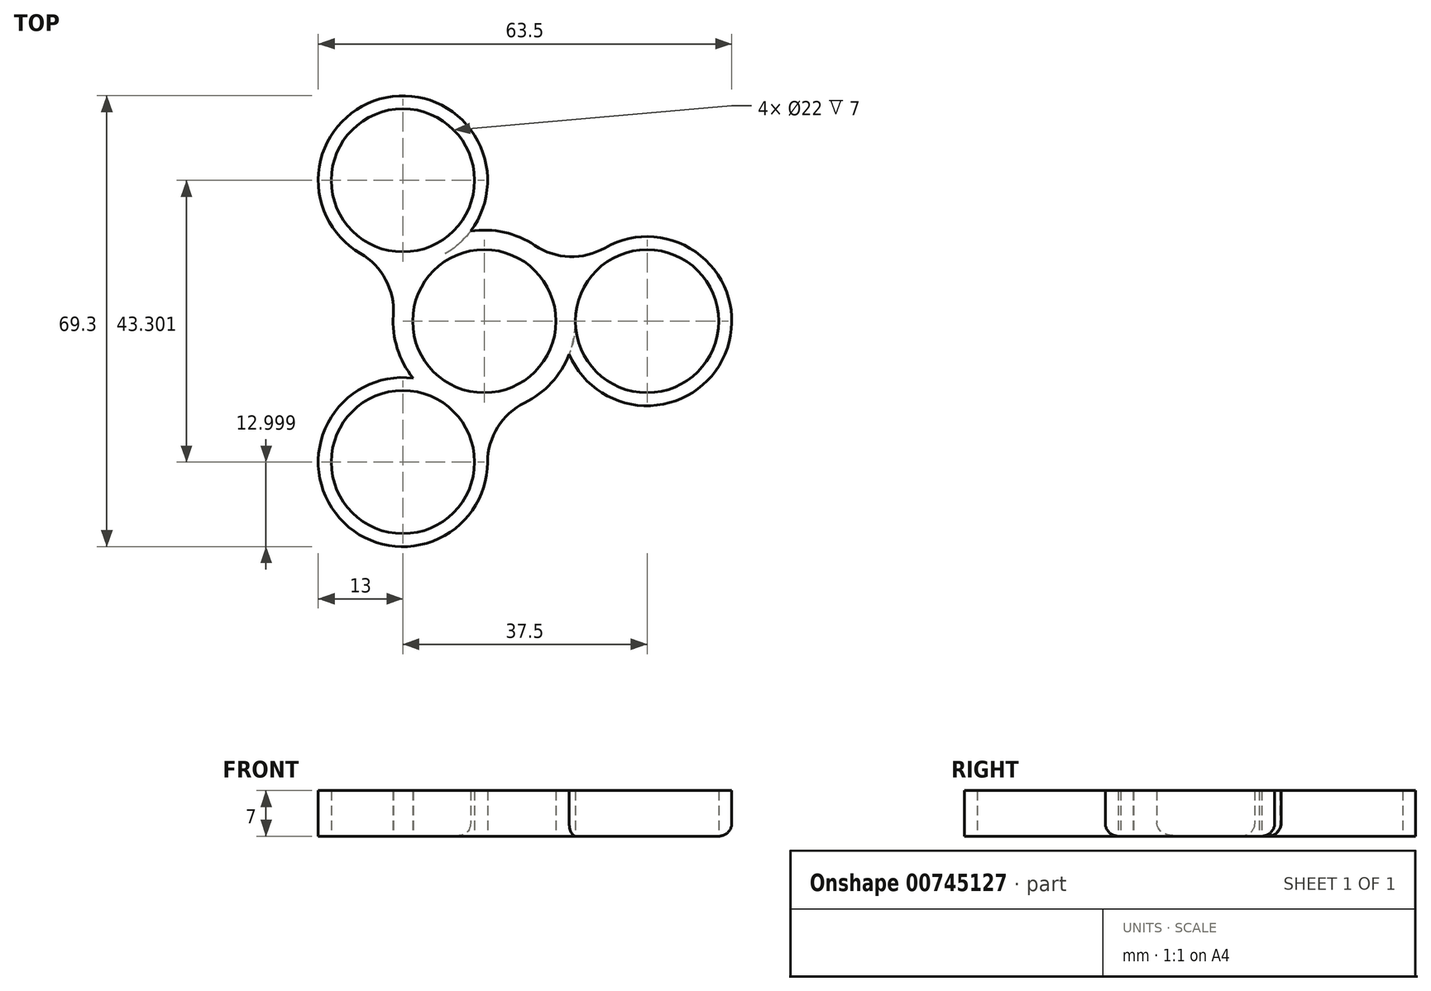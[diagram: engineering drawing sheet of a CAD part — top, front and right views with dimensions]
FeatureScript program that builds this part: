
annotation { "Feature Type Name" : "Feature", "Feature Type Description" : "" }
export const myFeature = defineFeature(function(context is Context, id is Id, definition is map)
    precondition{}
    {
        {
            var Q0;
            Q0=qCreatedBy(makeId("Top.planeOp"),FACE);
            var sketch = newSketch(context, id + "F0", { "sketchPlane" : qUnion([Q0])});
            skCircle(sketch, "E0", {"center": v(0, 0) * mm, "radius": 11 * mm});
            skCircle(sketch, "E1", {"center": v(25, 0) * mm, "radius": 11 * mm});
            skCircle(sketch, "E2.0", {"center": v(0, 0) * mm, "radius": 14 * mm});
            skCircle(sketch, "E3.0", {"center": v(25, 0) * mm, "radius": 13 * mm});
            skArc(sketch, "E4", {"start": v(7.78, 11.64) * mm, "mid": v(13.1, 9.92) * mm, "end": v(18.52, 11.27) * mm});
            skLineSegment(sketch, "E5", {"start": v(12, 0) * mm, "end": v(14, 0) * mm});
            skArc(sketch, "E6.MirrorCS", {"start": v(7.78, -11.64) * mm, "mid": v(13.1, -9.92) * mm, "end": v(18.52, -11.27) * mm});
            skSolve(sketch);
        }
        {
            var Q0;
            Q0=makeQuery(id+"F0.imprint","IMPRINT",FACE,{"disambiguationData":[TD([[makeQuery(id+"F0.imprint","IMPRINT",EDGE,{"derivedFrom":sQuery(id+"F0.wireOp",EDGE,"E0")}),-1.0]])]});
            var Q1;
            {var subQ0=sQuery(id+"F0.wireOp",EDGE,"E4");Q1=makeQuery(id+"F0.imprint","IMPRINT",FACE,{"disambiguationData":[TD([[makeQuery(id+"F0.imprint","IMPRINT",EDGE,{"derivedFrom":subQ0}),-1.0]])]});}
            var Q2;
            Q2=makeQuery(id+"F0.imprint","IMPRINT",FACE,{"disambiguationData":[TD([[makeQuery(id+"F0.imprint","IMPRINT",EDGE,{"derivedFrom":sQuery(id+"F0.wireOp",EDGE,"E1")}),-1.0]])]});
            var Q3;
            {var subQ0=sQuery(id+"F0.wireOp",EDGE,"E6.MirrorCS");Q3=makeQuery(id+"F0.imprint","IMPRINT",FACE,{"disambiguationData":[TD([[makeQuery(id+"F0.imprint","IMPRINT",EDGE,{"derivedFrom":subQ0}),1.0]])]});}
            var Q4;
            {var subQ2=sQuery(id+"F0.wireOp",EDGE,"E2.0");var subQ4=sQuery(id+"F0.wireOp",EDGE,"E1");var subQ7=makeQuery(id+"F0.imprint","INTERSECT",VERTEX,{"disambiguationData":[OD(0.0)],"derivedFrom":[subQ4,subQ2]});Q4=makeQuery(id+"F0.imprint","IMPRINT",FACE,{"disambiguationData":[TD([[makeQuery(id+"F0.imprint","IMPRINT",EDGE,{"disambiguationData":[TD([[subQ7,1.0]])],"derivedFrom":subQ4}),-1.0]])]});}
            var Q5;
            {var subQ0=sQuery(id+"F0.wireOp",EDGE,"E5");Q5=makeQuery(id+"F0.imprint","IMPRINT",FACE,{"disambiguationData":[TD([[makeQuery(id+"F0.imprint","IMPRINT",EDGE,{"derivedFrom":subQ0}),1.0]])]});}
            var Q6;
            {var subQ0=sQuery(id+"F0.wireOp",EDGE,"E5");Q6=makeQuery(id+"F0.imprint","IMPRINT",FACE,{"disambiguationData":[TD([[makeQuery(id+"F0.imprint","IMPRINT",EDGE,{"derivedFrom":subQ0}),-1.0]])]});}
            extrude(context, id + "F1", {"entities" : qUnion([Q0, Q1, Q2, Q3, Q4, Q5, Q6]), "depth" : 7 * mm, "offsetDistance" : 25 * mm});
        }
        {
            var Q0;
            Q0=makeQuery(id+"F1.opExtrude","SWEPT_BODY",BODY,{"disambiguationData":[OSD([sQuery(id+"F0.wireOp",EDGE,"E0"),sQuery(id+"F0.wireOp",EDGE,"E1"),sQuery(id+"F0.wireOp",EDGE,"E2.0"),sQuery(id+"F0.wireOp",EDGE,"E3.0"),sQuery(id+"F0.wireOp",EDGE,"E4"),sQuery(id+"F0.wireOp",EDGE,"E6.MirrorCS")])]});
            var Q1;
            Q1=makeQuery(id+"F1.opExtrude","CAP_EDGE",EDGE,{"disambiguationData":[OSD([sQuery(id+"F0.wireOp",EDGE,"E0")])],"isStart":true});
            circularPattern(context, id + "F2", {"operationType" : NewBodyOperationType.ADD, "entities" : qUnion([Q0]), "axis" : qUnion([Q1]), "angle" : 360 * degree, "instanceCount" : 3, "equalSpace" : true});
        }
        {
            var Q0;
            {var subQ0=sQuery(id+"F0.wireOp",EDGE,"E6.MirrorCS");var subQ2=sQuery(id+"F0.wireOp",EDGE,"E2.0");Q0=makeQuery(id+"F2.boolean.opBoolean","SPLIT",EDGE,{"disambiguationData":[TD([makeQuery(id+"F1.opExtrude","SWEPT_FACE",FACE,{"disambiguationData":[OSD([subQ0])]})])],"derivedFrom":makeQuery(id+"F1.opExtrude","CAP_EDGE",EDGE,{"disambiguationData":[OSD([subQ2])],"isStart":false})});}
            var Q1;
            {var subQ1=sQuery(id+"F0.wireOp",EDGE,"E4");var subQ2=sQuery(id+"F0.wireOp",EDGE,"E2.0");Q1=makeQuery(id+"F2.boolean.opBoolean","SPLIT",EDGE,{"disambiguationData":[TD([makeQuery(id+"F1.opExtrude","SWEPT_FACE",FACE,{"disambiguationData":[OSD([subQ1])]})])],"derivedFrom":makeQuery(id+"F1.opExtrude","CAP_EDGE",EDGE,{"disambiguationData":[OSD([subQ2])],"isStart":true})});}
            fillet(context, id + "F3", {"entities" : qUnion([Q0, Q1]), "radius" : 2 * mm, "tangentPropagation" : true, "allowEdgeOverflow" : false});
        }
    });
